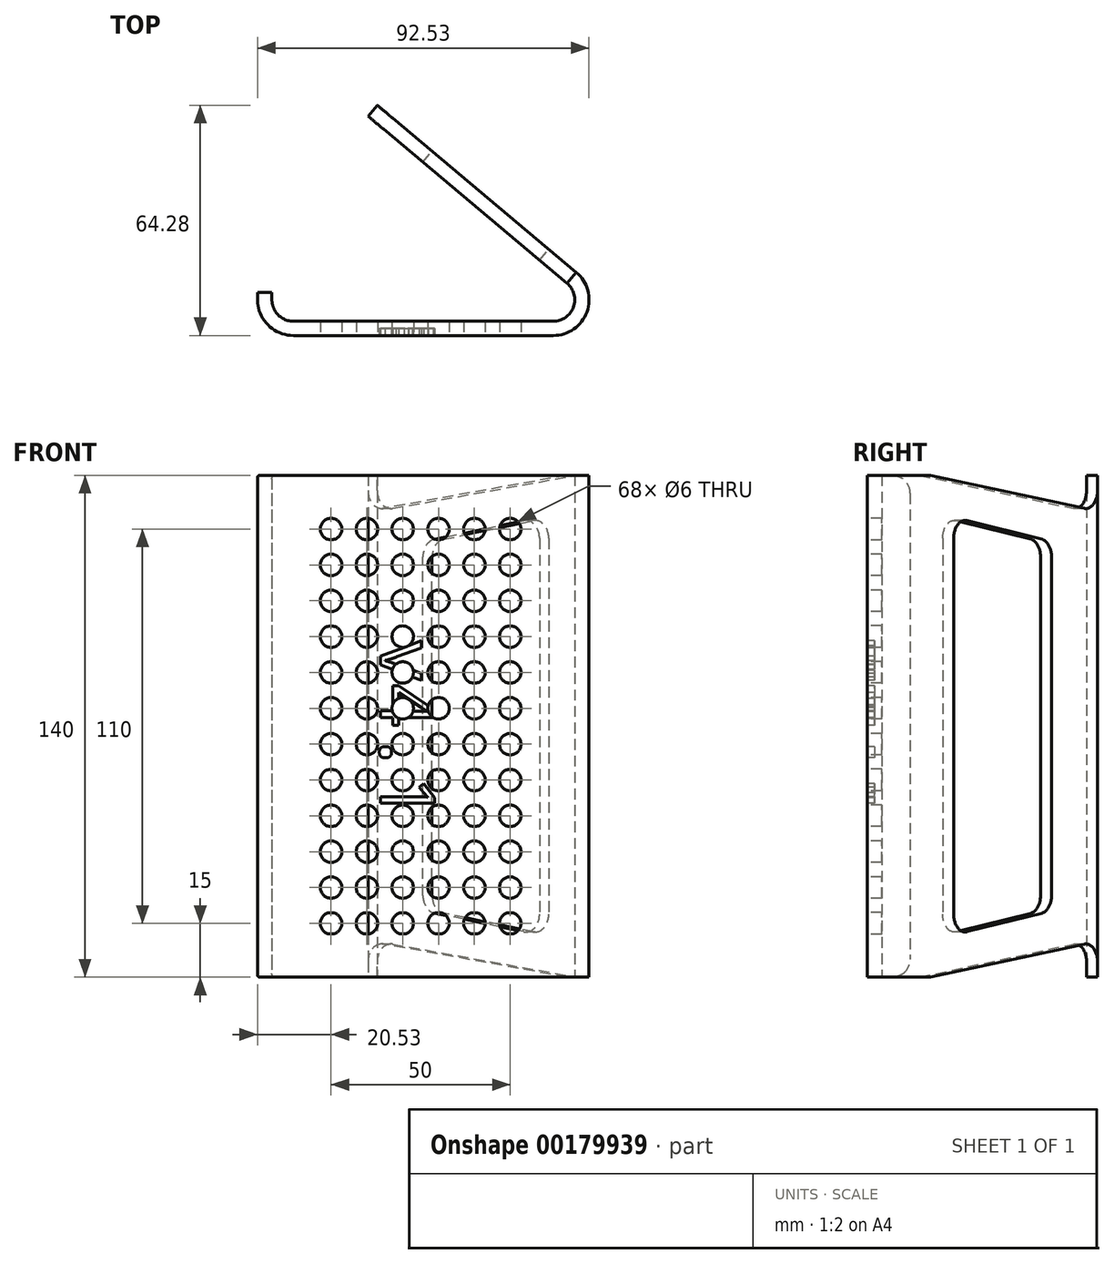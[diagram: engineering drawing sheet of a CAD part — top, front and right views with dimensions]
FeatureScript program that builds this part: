
annotation { "Feature Type Name" : "Feature", "Feature Type Description" : "" }
export const myFeature = defineFeature(function(context is Context, id is Id, definition is map)
    precondition{}
    {
        {
            var Q0;
            Q0=qCreatedBy(makeId("Top.planeOp"),FACE);
            var sketch = newSketch(context, id + "F0", { "sketchPlane" : qUnion([Q0])});
            skLineSegment(sketch, "E0", {"start": v(-43.59, -46.04) * mm, "end": v(28.94, -46.04) * mm});
            skLineSegment(sketch, "E1", {"start": v(-53.59, -36.04) * mm, "end": v(-53.59, -34.04) * mm});
            skPoint(sketch, "E2.visualSharp", {"position": v(-53.59, -46.04) * mm});
            skArc(sketch, "E2.filletArc", {"start": v(-53.59, -36.04) * mm, "mid": v(-50.66, -43.11) * mm, "end": v(-43.59, -46.04) * mm});
            skLineSegment(sketch, "E3", {"start": v(35.37, -28.38) * mm, "end": v(-20.2, 18.24) * mm});
            skPoint(sketch, "E4.visualSharp", {"position": v(56.41, -46.04) * mm});
            skArc(sketch, "E4.filletArc", {"start": v(28.94, -46.04) * mm, "mid": v(38.34, -39.46) * mm, "end": v(35.37, -28.38) * mm});
            skLineSegment(sketch, "E5.0", {"start": v(32.8, -31.44) * mm, "end": v(-22.76, 15.17) * mm});
            skLineSegment(sketch, "E5.1", {"start": v(-49.59, -36.04) * mm, "end": v(-49.59, -34.04) * mm});
            skArc(sketch, "E5.2", {"start": v(-49.59, -36.04) * mm, "mid": v(-47.83, -40.28) * mm, "end": v(-43.59, -42.04) * mm});
            skLineSegment(sketch, "E5.3", {"start": v(-43.59, -42.04) * mm, "end": v(28.94, -42.04) * mm});
            skArc(sketch, "E5.4", {"start": v(28.94, -42.04) * mm, "mid": v(34.58, -38.1) * mm, "end": v(32.8, -31.44) * mm});
            skLineSegment(sketch, "E6", {"start": v(-49.59, -34.04) * mm, "end": v(-53.59, -34.04) * mm});
            skLineSegment(sketch, "E7", {"start": v(-20.2, 18.24) * mm, "end": v(-22.76, 15.17) * mm});
            skSolve(sketch);
        }
        {
            var Q0;
            Q0=makeQuery(id+"F0.imprint","IMPRINT",FACE,{"disambiguationData":[TD([[makeQuery(id+"F0.imprint","IMPRINT",EDGE,{"derivedFrom":sQuery(id+"F0.wireOp",EDGE,"E0")}),1.0]])]});
            extrude(context, id + "F1", {"entities" : qUnion([Q0]), "depth" : 140 * mm});
        }
        {
            var Q0;
            Q0=makeQuery(id+"F1.opExtrude","CAP_EDGE",EDGE,{"disambiguationData":[OSD([sQuery(id+"F0.wireOp",EDGE,"E6")])],"isStart":true});
            fillet(context, id + "F2", {"entities" : qUnion([Q0]), "radius" : 5 * mm, "tangentPropagation" : true, "allowEdgeOverflow" : false});
        }
        {
            var Q0;
            Q0=makeQuery(id+"F1.opExtrude","CAP_EDGE",EDGE,{"disambiguationData":[OSD([sQuery(id+"F0.wireOp",EDGE,"E6")])],"isStart":false});
            fillet(context, id + "F3", {"entities" : qUnion([Q0]), "radius" : 5 * mm, "tangentPropagation" : true, "allowEdgeOverflow" : false});
        }
        {
            var Q0;
            Q0=makeQuery(id+"F1.opExtrude","SWEPT_FACE",FACE,{"disambiguationData":[OSD([sQuery(id+"F0.wireOp",EDGE,"E5.0")])]});
            var sketch = newSketch(context, id + "F4", { "sketchPlane" : qUnion([Q0])});
            skLineSegment(sketch, "E8", {"start": v(45.33, 0) * mm, "end": v(-27.2, 10) * mm});
            skLineSegment(sketch, "E9", {"start": v(45.33, 140) * mm, "end": v(-27.2, 130) * mm});
            skSolve(sketch);
        }
        {
            var Q0;
            {var subQ0=sQuery(id+"F4.wireOp",EDGE,"E8");Q0=makeQuery(id+"F4.imprint","IMPRINT",FACE,{"disambiguationData":[TD([[makeQuery(id+"F4.imprint","IMPRINT",EDGE,{"derivedFrom":subQ0}),1.0]])]});}
            var Q1;
            {var subQ0=sQuery(id+"F4.wireOp",EDGE,"E9");Q1=makeQuery(id+"F4.imprint","IMPRINT",FACE,{"disambiguationData":[TD([[makeQuery(id+"F4.imprint","IMPRINT",EDGE,{"derivedFrom":subQ0}),-1.0]])]});}
            extrude(context, id + "F5", {"entities" : qUnion([Q0, Q1]), "operationType" : NewBodyOperationType.REMOVE, "endBound" : BoundingType.UP_TO_NEXT, "oppositeDirection" : true, "depth" : 25 * mm});
        }
        {
            var Q0;
            Q0=makeQuery(id+"F5.boolean.opBoolean","COPY",EDGE,{"derivedFrom":makeQuery(id+"F5.opExtrude","SWEPT_EDGE",EDGE,{"disambiguationData":[OSD([sQuery(id+"F0.wireOp",EDGE,"E5.0"),sQuery(id+"F0.wireOp",EDGE,"E7"),sQuery(id+"F4.wireOp",EDGE,"E8")])]})});
            var Q1;
            Q1=makeQuery(id+"F5.boolean.opBoolean","COPY",EDGE,{"derivedFrom":makeQuery(id+"F5.opExtrude","SWEPT_EDGE",EDGE,{"disambiguationData":[OSD([sQuery(id+"F0.wireOp",EDGE,"E5.0"),sQuery(id+"F0.wireOp",EDGE,"E7"),sQuery(id+"F4.wireOp",EDGE,"E9")])]})});
            fillet(context, id + "F6", {"entities" : qUnion([Q0, Q1]), "radius" : 5 * mm, "tangentPropagation" : true, "allowEdgeOverflow" : false});
        }
        {
            var Q0;
            Q0=makeQuery(id+"F1.opExtrude","SWEPT_FACE",FACE,{"disambiguationData":[OSD([sQuery(id+"F0.wireOp",EDGE,"E0")])]});
            var sketch = newSketch(context, id + "F7", { "sketchPlane" : qUnion([Q0])});
            skText(sketch, "E10", { "text": "v4.1", "fontName": "DroidSansMono.ttf"});
            const initialGuessF7  = {"E10": [-0.0193, 0.09468, 0, -1, 0.01532]};
            skSetInitialGuess(sketch, initialGuessF7);
            skSolve(sketch);
        }
        {
            var Q0;
            Q0 = qSketchRegion(id + "F7", true);
            extrude(context, id + "F8", {"entities" : qUnion([Q0]), "operationType" : NewBodyOperationType.REMOVE, "oppositeDirection" : true, "depth" : 2 * mm});
        }
        {
            var Q0;
            Q0=makeQuery(id+"F1.opExtrude","SWEPT_FACE",FACE,{"disambiguationData":[OSD([sQuery(id+"F0.wireOp",EDGE,"E5.3")])]});
            var sketch = newSketch(context, id + "F9", { "sketchPlane" : qUnion([Q0])});
            skCircle(sketch, "E11", {"center": v(-16.94, 15) * mm, "radius": 2 * mm});
            skCircle(sketch, "E12.0.1.0", {"center": v(-16.94, 25) * mm, "radius": 2 * mm});
            skCircle(sketch, "E12.0.2.0", {"center": v(-16.94, 35) * mm, "radius": 2 * mm});
            skCircle(sketch, "E12.0.3.0", {"center": v(-16.94, 45) * mm, "radius": 2 * mm});
            skCircle(sketch, "E12.0.4.0", {"center": v(-16.94, 55) * mm, "radius": 2 * mm});
            skCircle(sketch, "E12.0.5.0", {"center": v(-16.94, 65) * mm, "radius": 2 * mm});
            skCircle(sketch, "E12.0.6.0", {"center": v(-16.94, 75) * mm, "radius": 2 * mm});
            skCircle(sketch, "E12.0.7.0", {"center": v(-16.94, 85) * mm, "radius": 2 * mm});
            skCircle(sketch, "E12.0.8.0", {"center": v(-16.94, 95) * mm, "radius": 2 * mm});
            skCircle(sketch, "E12.0.9.0", {"center": v(-16.94, 105) * mm, "radius": 2 * mm});
            skCircle(sketch, "E12.0.10.0", {"center": v(-16.94, 115) * mm, "radius": 2 * mm});
            skCircle(sketch, "E12.0.11.0", {"center": v(-16.94, 125) * mm, "radius": 2 * mm});
            skCircle(sketch, "E12.1.0.0", {"center": v(-6.94, 15) * mm, "radius": 2 * mm});
            skCircle(sketch, "E12.1.1.0", {"center": v(-6.94, 25) * mm, "radius": 2 * mm});
            skCircle(sketch, "E12.1.2.0", {"center": v(-6.94, 35) * mm, "radius": 2 * mm});
            skCircle(sketch, "E12.1.3.0", {"center": v(-6.94, 45) * mm, "radius": 2 * mm});
            skCircle(sketch, "E12.1.4.0", {"center": v(-6.94, 55) * mm, "radius": 2 * mm});
            skCircle(sketch, "E12.1.5.0", {"center": v(-6.94, 65) * mm, "radius": 2 * mm});
            skCircle(sketch, "E12.1.6.0", {"center": v(-6.94, 75) * mm, "radius": 2 * mm});
            skCircle(sketch, "E12.1.7.0", {"center": v(-6.94, 85) * mm, "radius": 2 * mm});
            skCircle(sketch, "E12.1.8.0", {"center": v(-6.94, 95) * mm, "radius": 2 * mm});
            skCircle(sketch, "E12.1.9.0", {"center": v(-6.94, 105) * mm, "radius": 2 * mm});
            skCircle(sketch, "E12.1.10.0", {"center": v(-6.94, 115) * mm, "radius": 2 * mm});
            skCircle(sketch, "E12.1.11.0", {"center": v(-6.94, 125) * mm, "radius": 2 * mm});
            skCircle(sketch, "E12.2.0.0", {"center": v(3.06, 15) * mm, "radius": 2 * mm});
            skCircle(sketch, "E12.2.1.0", {"center": v(3.06, 25) * mm, "radius": 2 * mm});
            skCircle(sketch, "E12.2.2.0", {"center": v(3.06, 35) * mm, "radius": 2 * mm});
            skCircle(sketch, "E12.2.3.0", {"center": v(3.06, 45) * mm, "radius": 2 * mm});
            skCircle(sketch, "E12.2.4.0", {"center": v(3.06, 55) * mm, "radius": 2 * mm});
            skCircle(sketch, "E12.2.5.0", {"center": v(3.06, 65) * mm, "radius": 2 * mm});
            skCircle(sketch, "E12.2.6.0", {"center": v(3.06, 75) * mm, "radius": 2 * mm});
            skCircle(sketch, "E12.2.7.0", {"center": v(3.06, 85) * mm, "radius": 2 * mm});
            skCircle(sketch, "E12.2.8.0", {"center": v(3.06, 95) * mm, "radius": 2 * mm});
            skCircle(sketch, "E12.2.9.0", {"center": v(3.06, 105) * mm, "radius": 2 * mm});
            skCircle(sketch, "E12.2.10.0", {"center": v(3.06, 115) * mm, "radius": 2 * mm});
            skCircle(sketch, "E12.2.11.0", {"center": v(3.06, 125) * mm, "radius": 2 * mm});
            skCircle(sketch, "E12.3.0.0", {"center": v(13.06, 15) * mm, "radius": 2 * mm});
            skCircle(sketch, "E12.3.1.0", {"center": v(13.06, 25) * mm, "radius": 2 * mm});
            skCircle(sketch, "E12.3.2.0", {"center": v(13.06, 35) * mm, "radius": 2 * mm});
            skCircle(sketch, "E12.3.3.0", {"center": v(13.06, 45) * mm, "radius": 2 * mm});
            skCircle(sketch, "E12.3.4.0", {"center": v(13.06, 55) * mm, "radius": 2 * mm});
            skCircle(sketch, "E12.3.5.0", {"center": v(13.06, 65) * mm, "radius": 2 * mm});
            skCircle(sketch, "E12.3.6.0", {"center": v(13.06, 75) * mm, "radius": 2 * mm});
            skCircle(sketch, "E12.3.7.0", {"center": v(13.06, 85) * mm, "radius": 2 * mm});
            skCircle(sketch, "E12.3.8.0", {"center": v(13.06, 95) * mm, "radius": 2 * mm});
            skCircle(sketch, "E12.3.9.0", {"center": v(13.06, 105) * mm, "radius": 2 * mm});
            skCircle(sketch, "E12.3.10.0", {"center": v(13.06, 115) * mm, "radius": 2 * mm});
            skCircle(sketch, "E12.3.11.0", {"center": v(13.06, 125) * mm, "radius": 2 * mm});
            skCircle(sketch, "E12.4.0.0", {"center": v(23.06, 15) * mm, "radius": 2 * mm});
            skCircle(sketch, "E12.4.1.0", {"center": v(23.06, 25) * mm, "radius": 2 * mm});
            skCircle(sketch, "E12.4.2.0", {"center": v(23.06, 35) * mm, "radius": 2 * mm});
            skCircle(sketch, "E12.4.3.0", {"center": v(23.06, 45) * mm, "radius": 2 * mm});
            skCircle(sketch, "E12.4.4.0", {"center": v(23.06, 55) * mm, "radius": 2 * mm});
            skCircle(sketch, "E12.4.5.0", {"center": v(23.06, 65) * mm, "radius": 2 * mm});
            skCircle(sketch, "E12.4.6.0", {"center": v(23.06, 75) * mm, "radius": 2 * mm});
            skCircle(sketch, "E12.4.7.0", {"center": v(23.06, 85) * mm, "radius": 2 * mm});
            skCircle(sketch, "E12.4.8.0", {"center": v(23.06, 95) * mm, "radius": 2 * mm});
            skCircle(sketch, "E12.4.9.0", {"center": v(23.06, 105) * mm, "radius": 2 * mm});
            skCircle(sketch, "E12.4.10.0", {"center": v(23.06, 115) * mm, "radius": 2 * mm});
            skCircle(sketch, "E12.4.11.0", {"center": v(23.06, 125) * mm, "radius": 2 * mm});
            skCircle(sketch, "E12.5.0.0", {"center": v(33.06, 15) * mm, "radius": 2 * mm});
            skCircle(sketch, "E12.5.1.0", {"center": v(33.06, 25) * mm, "radius": 2 * mm});
            skCircle(sketch, "E12.5.2.0", {"center": v(33.06, 35) * mm, "radius": 2 * mm});
            skCircle(sketch, "E12.5.3.0", {"center": v(33.06, 45) * mm, "radius": 2 * mm});
            skCircle(sketch, "E12.5.4.0", {"center": v(33.06, 55) * mm, "radius": 2 * mm});
            skCircle(sketch, "E12.5.5.0", {"center": v(33.06, 65) * mm, "radius": 2 * mm});
            skCircle(sketch, "E12.5.6.0", {"center": v(33.06, 75) * mm, "radius": 2 * mm});
            skCircle(sketch, "E12.5.7.0", {"center": v(33.06, 85) * mm, "radius": 2 * mm});
            skCircle(sketch, "E12.5.8.0", {"center": v(33.06, 95) * mm, "radius": 2 * mm});
            skCircle(sketch, "E12.5.9.0", {"center": v(33.06, 105) * mm, "radius": 2 * mm});
            skCircle(sketch, "E12.5.10.0", {"center": v(33.06, 115) * mm, "radius": 2 * mm});
            skCircle(sketch, "E12.5.11.0", {"center": v(33.06, 125) * mm, "radius": 2 * mm});
            skLineSegment(sketch, "E12.direction1", {"start": v(-16.94, 15) * mm, "end": v(-6.94, 15) * mm, "construction": true});
            skLineSegment(sketch, "E12.direction2", {"start": v(-16.94, 15) * mm, "end": v(-16.94, 25) * mm, "construction": true});
            skSolve(sketch);
        }
        {
            var Q0;
            Q0=sQuery(id+"F9.wireOp",VERTEX,"E12.direction1.start");
            var Q1;
            Q1=sQuery(id+"F9.wireOp",VERTEX,"E12.1.0.0.center");
            var Q2;
            Q2=sQuery(id+"F9.wireOp",VERTEX,"E12.2.0.0.center");
            var Q3;
            Q3=sQuery(id+"F9.wireOp",VERTEX,"E12.3.0.0.center");
            var Q4;
            Q4=sQuery(id+"F9.wireOp",VERTEX,"E12.4.0.0.center");
            var Q5;
            Q5=sQuery(id+"F9.wireOp",VERTEX,"E12.5.0.0.center");
            var Q6;
            Q6=sQuery(id+"F9.wireOp",VERTEX,"E12.5.1.0.center");
            var Q7;
            Q7=sQuery(id+"F9.wireOp",VERTEX,"E12.4.1.0.center");
            var Q8;
            Q8=sQuery(id+"F9.wireOp",VERTEX,"E12.3.1.0.center");
            var Q9;
            Q9=sQuery(id+"F9.wireOp",VERTEX,"E12.3.2.0.center");
            var Q10;
            Q10=sQuery(id+"F9.wireOp",VERTEX,"E12.2.2.0.center");
            var Q11;
            Q11=sQuery(id+"F9.wireOp",VERTEX,"E12.2.1.0.center");
            var Q12;
            Q12=sQuery(id+"F9.wireOp",VERTEX,"E12.1.1.0.center");
            var Q13;
            Q13=sQuery(id+"F9.wireOp",VERTEX,"E12.0.1.0.center");
            var Q14;
            Q14=sQuery(id+"F9.wireOp",VERTEX,"E12.0.2.0.center");
            var Q15;
            Q15=sQuery(id+"F9.wireOp",VERTEX,"E12.1.2.0.center");
            var Q16;
            Q16=sQuery(id+"F9.wireOp",VERTEX,"E12.4.2.0.center");
            var Q17;
            Q17=sQuery(id+"F9.wireOp",VERTEX,"E12.5.2.0.center");
            var Q18;
            Q18=sQuery(id+"F9.wireOp",VERTEX,"E12.5.3.0.center");
            var Q19;
            Q19=sQuery(id+"F9.wireOp",VERTEX,"E12.4.3.0.center");
            var Q20;
            Q20=sQuery(id+"F9.wireOp",VERTEX,"E12.3.3.0.center");
            var Q21;
            Q21=sQuery(id+"F9.wireOp",VERTEX,"E12.2.3.0.center");
            var Q22;
            Q22=sQuery(id+"F9.wireOp",VERTEX,"E12.1.3.0.center");
            var Q23;
            Q23=sQuery(id+"F9.wireOp",VERTEX,"E12.0.3.0.center");
            var Q24;
            Q24=sQuery(id+"F9.wireOp",VERTEX,"E12.2.9.0.center");
            var Q25;
            Q25=sQuery(id+"F9.wireOp",VERTEX,"E12.5.4.0.center");
            var Q26;
            Q26=sQuery(id+"F9.wireOp",VERTEX,"E12.5.5.0.center");
            var Q27;
            Q27=sQuery(id+"F9.wireOp",VERTEX,"E12.4.4.0.center");
            var Q28;
            Q28=sQuery(id+"F9.wireOp",VERTEX,"E12.4.5.0.center");
            var Q29;
            Q29=sQuery(id+"F9.wireOp",VERTEX,"E12.3.5.0.center");
            var Q30;
            Q30=sQuery(id+"F9.wireOp",VERTEX,"E12.3.6.0.center");
            var Q31;
            Q31=sQuery(id+"F9.wireOp",VERTEX,"E12.3.7.0.center");
            var Q32;
            Q32=sQuery(id+"F9.wireOp",VERTEX,"E12.3.8.0.center");
            var Q33;
            Q33=sQuery(id+"F9.wireOp",VERTEX,"E12.3.9.0.center");
            var Q34;
            Q34=sQuery(id+"F9.wireOp",VERTEX,"E12.4.8.0.center");
            var Q35;
            Q35=sQuery(id+"F9.wireOp",VERTEX,"E12.5.7.0.center");
            var Q36;
            Q36=sQuery(id+"F9.wireOp",VERTEX,"E12.4.7.0.center");
            var Q37;
            Q37=sQuery(id+"F9.wireOp",VERTEX,"E12.5.6.0.center");
            var Q38;
            Q38=sQuery(id+"F9.wireOp",VERTEX,"E12.4.6.0.center");
            var Q39;
            Q39=sQuery(id+"F9.wireOp",VERTEX,"E12.0.4.0.center");
            var Q40;
            Q40=sQuery(id+"F9.wireOp",VERTEX,"E12.1.4.0.center");
            var Q41;
            Q41=sQuery(id+"F9.wireOp",VERTEX,"E12.2.4.0.center");
            var Q42;
            Q42=sQuery(id+"F9.wireOp",VERTEX,"E12.3.4.0.center");
            var Q43;
            Q43=sQuery(id+"F9.wireOp",VERTEX,"E12.2.5.0.center");
            var Q44;
            Q44=sQuery(id+"F9.wireOp",VERTEX,"E12.1.6.0.center");
            var Q45;
            Q45=sQuery(id+"F9.wireOp",VERTEX,"E12.0.7.0.center");
            var Q46;
            Q46=sQuery(id+"F9.wireOp",VERTEX,"E12.1.7.0.center");
            var Q47;
            Q47=sQuery(id+"F9.wireOp",VERTEX,"E12.2.7.0.center");
            var Q48;
            Q48=sQuery(id+"F9.wireOp",VERTEX,"E12.2.6.0.center");
            var Q49;
            Q49=sQuery(id+"F9.wireOp",VERTEX,"E12.1.5.0.center");
            var Q50;
            Q50=sQuery(id+"F9.wireOp",VERTEX,"E12.0.6.0.center");
            var Q51;
            Q51=sQuery(id+"F9.wireOp",VERTEX,"E12.0.5.0.center");
            var Q52;
            Q52=sQuery(id+"F9.wireOp",VERTEX,"E12.2.8.0.center");
            var Q53;
            Q53=sQuery(id+"F9.wireOp",VERTEX,"E12.5.8.0.center");
            var Q54;
            Q54=sQuery(id+"F9.wireOp",VERTEX,"E12.4.9.0.center");
            var Q55;
            Q55=sQuery(id+"F9.wireOp",VERTEX,"E12.5.9.0.center");
            var Q56;
            Q56=sQuery(id+"F9.wireOp",VERTEX,"E12.5.10.0.center");
            var Q57;
            Q57=sQuery(id+"F9.wireOp",VERTEX,"E12.5.11.0.center");
            var Q58;
            Q58=sQuery(id+"F9.wireOp",VERTEX,"E12.4.11.0.center");
            var Q59;
            Q59=sQuery(id+"F9.wireOp",VERTEX,"E12.4.10.0.center");
            var Q60;
            Q60=sQuery(id+"F9.wireOp",VERTEX,"E12.2.10.0.center");
            var Q61;
            Q61=sQuery(id+"F9.wireOp",VERTEX,"E12.3.10.0.center");
            var Q62;
            Q62=sQuery(id+"F9.wireOp",VERTEX,"E12.3.11.0.center");
            var Q63;
            Q63=sQuery(id+"F9.wireOp",VERTEX,"E12.2.11.0.center");
            var Q64;
            Q64=sQuery(id+"F9.wireOp",VERTEX,"E12.1.11.0.center");
            var Q65;
            Q65=sQuery(id+"F9.wireOp",VERTEX,"E12.0.11.0.center");
            var Q66;
            Q66=sQuery(id+"F9.wireOp",VERTEX,"E12.1.10.0.center");
            var Q67;
            Q67=sQuery(id+"F9.wireOp",VERTEX,"E12.0.10.0.center");
            var Q68;
            Q68=sQuery(id+"F9.wireOp",VERTEX,"E12.1.9.0.center");
            var Q69;
            Q69=sQuery(id+"F9.wireOp",VERTEX,"E12.0.9.0.center");
            var Q70;
            Q70=sQuery(id+"F9.wireOp",VERTEX,"E12.0.8.0.center");
            var Q71;
            Q71=sQuery(id+"F9.wireOp",VERTEX,"E12.1.8.0.center");
            var Q72;
            Q72=makeQuery(id+"F1.opExtrude","SWEPT_BODY",BODY,{"disambiguationData":[OSD([sQuery(id+"F0.wireOp",EDGE,"E0"),sQuery(id+"F0.wireOp",EDGE,"E1"),sQuery(id+"F0.wireOp",EDGE,"E2.filletArc"),sQuery(id+"F0.wireOp",EDGE,"E3"),sQuery(id+"F0.wireOp",EDGE,"E4.filletArc"),sQuery(id+"F0.wireOp",EDGE,"E5.0"),sQuery(id+"F0.wireOp",EDGE,"E5.1"),sQuery(id+"F0.wireOp",EDGE,"E5.2"),sQuery(id+"F0.wireOp",EDGE,"E5.3"),sQuery(id+"F0.wireOp",EDGE,"E5.4"),sQuery(id+"F0.wireOp",EDGE,"E6"),sQuery(id+"F0.wireOp",EDGE,"E7")])]});
            hole(context, id + "F10", {"style" : HoleStyle.SIMPLE, "endStyle" : HoleEndStyle.BLIND, "holeDiameter" : 6 * mm, "majorDiameter" : 5 * mm, "holeDepth" : 20 * mm, "tappedDepth" : 12 * mm, "tapClearance" : 3, "locations" : qUnion([Q0, Q1, Q2, Q3, Q4, Q5, Q6, Q7, Q8, Q9, Q10, Q11, Q12, Q13, Q14, Q15, Q16, Q17, Q18, Q19, Q20, Q21, Q22, Q23, Q24, Q25, Q26, Q27, Q28, Q29, Q30, Q31, Q32, Q33, Q34, Q35, Q36, Q37, Q38, Q39, Q40, Q41, Q42, Q43, Q44, Q45, Q46, Q47, Q48, Q49, Q50, Q51, Q52, Q53, Q54, Q55, Q56, Q57, Q58, Q59, Q60, Q61, Q62, Q63, Q64, Q65, Q66, Q67, Q68, Q69, Q70, Q71]), "scope" : qUnion([Q72]), "startStyle" : HoleStartStyle.PART});
        }
        {
            var Q0;
            Q0=makeQuery(id+"F1.opExtrude","SWEPT_FACE",FACE,{"disambiguationData":[OSD([sQuery(id+"F0.wireOp",EDGE,"E3")])]});
            var sketch = newSketch(context, id + "F11", { "sketchPlane" : qUnion([Q0])});
            skLineSegment(sketch, "E13.0", {"start": v(-35.33, 11.73) * mm, "end": v(7.2, 18.53) * mm});
            skLineSegment(sketch, "E13.1", {"start": v(-35.33, 128.27) * mm, "end": v(-35.33, 11.73) * mm});
            skLineSegment(sketch, "E13.2", {"start": v(7.2, 121.47) * mm, "end": v(-35.33, 128.27) * mm});
            skLineSegment(sketch, "E13.3", {"start": v(7.2, 18.53) * mm, "end": v(7.2, 121.47) * mm});
            skSolve(sketch);
        }
        {
            var Q0;
            Q0=makeQuery(id+"F11.imprint","IMPRINT",FACE,{"disambiguationData":[TD([[makeQuery(id+"F11.imprint","IMPRINT",EDGE,{"derivedFrom":sQuery(id+"F11.wireOp",EDGE,"E13.0")}),1.0]])]});
            extrude(context, id + "F12", {"entities" : qUnion([Q0]), "operationType" : NewBodyOperationType.REMOVE, "endBound" : BoundingType.UP_TO_NEXT, "oppositeDirection" : true, "depth" : 25 * mm});
        }
        {
            var Q0;
            Q0=makeQuery(id+"F12.boolean.opBoolean","COPY",EDGE,{"derivedFrom":makeQuery(id+"F12.opExtrude","SWEPT_EDGE",EDGE,{"disambiguationData":[OSD([sQuery(id+"F11.wireOp",EDGE,"E13.0"),sQuery(id+"F11.wireOp",EDGE,"E13.3")])]})});
            var Q1;
            Q1=makeQuery(id+"F12.boolean.opBoolean","COPY",EDGE,{"derivedFrom":makeQuery(id+"F12.opExtrude","SWEPT_EDGE",EDGE,{"disambiguationData":[OSD([sQuery(id+"F11.wireOp",EDGE,"E13.2"),sQuery(id+"F11.wireOp",EDGE,"E13.3")])]})});
            var Q2;
            Q2=makeQuery(id+"F12.boolean.opBoolean","COPY",EDGE,{"derivedFrom":makeQuery(id+"F12.opExtrude","SWEPT_EDGE",EDGE,{"disambiguationData":[OSD([sQuery(id+"F11.wireOp",EDGE,"E13.0"),sQuery(id+"F11.wireOp",EDGE,"E13.1")])]})});
            var Q3;
            Q3=makeQuery(id+"F12.boolean.opBoolean","COPY",EDGE,{"derivedFrom":makeQuery(id+"F12.opExtrude","SWEPT_EDGE",EDGE,{"disambiguationData":[OSD([sQuery(id+"F11.wireOp",EDGE,"E13.1"),sQuery(id+"F11.wireOp",EDGE,"E13.2")])]})});
            fillet(context, id + "F13", {"entities" : qUnion([Q0, Q1, Q2, Q3]), "radius" : 5 * mm, "tangentPropagation" : true, "allowEdgeOverflow" : false});
        }
    });
